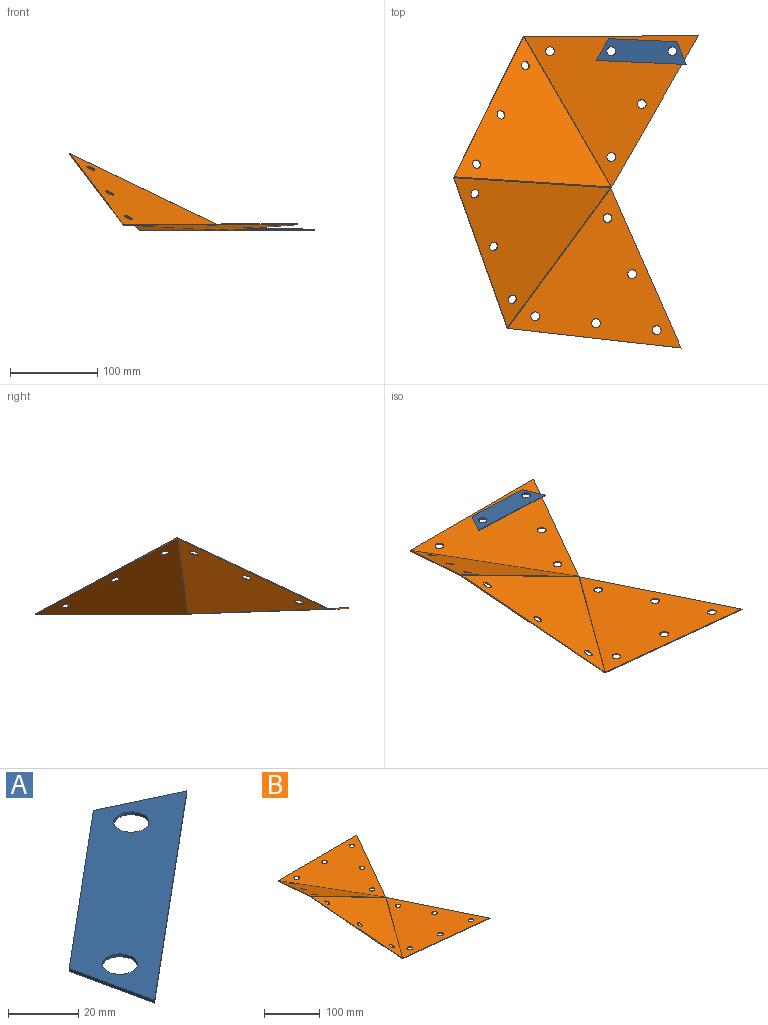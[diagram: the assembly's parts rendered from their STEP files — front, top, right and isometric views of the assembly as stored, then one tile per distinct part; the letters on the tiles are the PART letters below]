
ASSEMBLY  parts=2 mates=1
PART A: 8 faces, bbox 85.4x78.3x1 mm
  f0: plane 79.29x66.34mm, normal (0.64,-0.77,0), area 103.4mm2, adj f1,f4,f6,f7
  f1: plane 25.54x12mm, normal (0.43,0.91,0), area 28.2mm2, adj f0,f2,f6,f7
  f2: plane 59.9x50.18mm, normal (-0.64,0.77,0), area 78.1mm2, adj f1,f4,f6,f7
  f3: cylinder r=5mm len=10mm, axis (0,0,-1), area 31.4mm2, adj f6,f7
  f4: plane 28.16x6.15mm, normal (-0.98,-0.21,0), area 28.8mm2, adj f0,f2,f6,f7
  f5: cylinder r=5mm len=10mm, axis (0,0,-1), area 31.4mm2, adj f6,f7
  f6: plane 85.44x78.34mm, normal (0,0,1), area 2163.2mm2, adj f0,f1,f2,f3,f4,f5
  f7: plane 85.44x78.34mm, normal (0,0,-1), area 2163.2mm2, adj f0,f1,f2,f3,f4,f5
PART B: 46 faces, bbox 280.4x357.3x87.6 mm
  f0: plane 1x0.4mm, normal (-0.87,-0.5,0), area 0.5mm2, adj f1,f8,f9,f42
  f1: plane 173.03x99.68mm, normal (0.87,-0.5,0), area 199.7mm2, adj f0,f7,f8,f9
  f2: cylinder r=5mm len=10mm, axis (0,0,1), area 31.4mm2, adj f8,f9
  f3: cylinder r=5mm len=10mm, axis (0,0,1), area 31.4mm2, adj f8,f9
  f4: cylinder r=5mm len=10mm, axis (0,0,1), area 31.4mm2, adj f8,f9
  f5: cylinder r=5mm len=10mm, axis (0,0,1), area 31.4mm2, adj f8,f9
  f6: cylinder r=5mm len=10mm, axis (0,0,1), area 31.4mm2, adj f8,f9
  f7: plane 199.69x1mm, normal (0,1,0), area 199.7mm2, adj f1,f8,f9,f43
  f8: plane 199.69x173.03mm, normal (0,0,-1), area 16874.3mm2, adj f0,f1,f2,f3,f4,f5,f6,f7
  f9: plane 199.69x173.03mm, normal (0,0,1), area 16874.3mm2, adj f0,f1,f2,f3,f4,f5,f6,f7
  f10: plane 1.13x0.99mm, normal (0.06,-0.97,0.25), area 0.6mm2, adj f15,f16,f38,f42
  f11: plane 161.43x87.2mm, normal (-0.81,0.53,0.25), area 199.4mm2, adj f15,f16,f39,f43
  f12: cylinder r=5mm len=9.93mm, axis (-0.43,-0.25,-0.87), area 31.4mm2, adj f15,f16
  f13: cylinder r=5mm len=9.93mm, axis (-0.43,-0.25,-0.87), area 31.4mm2, adj f15,f16
  f14: cylinder r=5mm len=9.93mm, axis (-0.43,-0.25,-0.87), area 31.4mm2, adj f15,f16
  f15: plane 179.36x172.57mm, normal (-0.43,-0.25,-0.87), area 16977.9mm2, adj f10,f11,f12,f13,f14,f41,f44
  f16: plane 179.36x172.57mm, normal (0.43,0.25,0.87), area 16977.9mm2, adj f10,f11,f12,f13,f14,f40,f45
  f17: plane 1.01x0.68mm, normal (0.17,0.96,0.22), area 0.3mm2, adj f18,f19,f23,f39
  f18: plane 179.27x171.84mm, normal (0.4,-0.27,0.87), area 16977.9mm2, adj f17,f19,f20,f21,f22,f24,f37,f40
  f19: plane 172.1x81.43mm, normal (-0.86,-0.43,0.27), area 199.4mm2, adj f17,f18,f23,f34
  f20: cylinder r=5mm len=9.91mm, axis (-0.4,0.27,-0.87), area 31.4mm2, adj f18,f23
  f21: cylinder r=5mm len=9.91mm, axis (-0.4,0.27,-0.87), area 31.4mm2, adj f18,f23
  f22: cylinder r=5mm len=9.91mm, axis (-0.4,0.27,-0.87), area 31.4mm2, adj f18,f23
  f23: plane 179.27x171.84mm, normal (-0.4,0.27,-0.87), area 16977.9mm2, adj f17,f19,f20,f21,f22,f24,f36,f41
  f24: plane 1x0.59mm, normal (0.59,0.8,-0.03), area 0.3mm2, adj f18,f23,f35,f38
  f25: plane 183.01x80.5mm, normal (0.92,0.4,-0.02), area 200mm2, adj f26,f32,f33,f35
  f26: plane 198.73x22.57mm, normal (-0.11,-0.99,0.03), area 200mm2, adj f25,f32,f33,f34
  f27: cylinder r=5mm len=10.03mm, axis (0,-0.03,-1), area 31.4mm2, adj f32,f33
  f28: cylinder r=5mm len=10.03mm, axis (0,-0.03,-1), area 31.4mm2, adj f32,f33
  f29: cylinder r=5mm len=10.03mm, axis (0,-0.03,-1), area 31.4mm2, adj f32,f33
  f30: cylinder r=5mm len=10.03mm, axis (0,-0.03,-1), area 31.4mm2, adj f32,f33
  f31: cylinder r=5mm len=10.03mm, axis (0,-0.03,-1), area 31.4mm2, adj f32,f33
  f32: plane 198.73x182.98mm, normal (0,-0.03,-1), area 16892mm2, adj f25,f26,f27,f28,f29,f30,f31,f36
  f33: plane 198.73x182.98mm, normal (0,0.03,1), area 16892mm2, adj f25,f26,f27,f28,f29,f30,f31,f37
  f34: bspline ~1.12x0.73mm, area 0.8mm2, adj f19,f26,f36,f37
  f35: plane 1.12x0.81mm, normal (0.59,0.8,-0.03), area 0.8mm2, adj f24,f25,f36,f37
  f36: cylinder r=2mm len=161.05mm, axis (-0.59,-0.8,0.03), area 208.7mm2, adj f23,f32,f34,f35
  f37: cylinder r=1mm len=160.74mm, axis (-0.59,-0.8,0.03), area 104.4mm2, adj f18,f33,f34,f35
  f38: plane 1.03x0.94mm, normal (0.9,-0.06,-0.43), area 0.8mm2, adj f10,f24,f40,f41
  f39: plane 1.03x0.94mm, normal (-0.9,0.06,0.43), area 0.8mm2, adj f11,f17,f40,f41
  f40: cylinder r=2mm len=178.87mm, axis (0.9,-0.06,-0.43), area 208.1mm2, adj f16,f18,f38,f39
  f41: cylinder r=1mm len=178.83mm, axis (0.9,-0.06,-0.43), area 104.1mm2, adj f15,f23,f38,f39
  f42: plane 1.13x0.87mm, normal (0.5,-0.87,0), area 0.8mm2, adj f0,f10,f44,f45
  f43: bspline ~1.13x0.94mm, area 0.8mm2, adj f7,f11,f44,f45
  f44: cylinder r=2mm len=173.07mm, axis (0.5,-0.87,0), area 208.7mm2, adj f8,f15,f42,f43
  f45: cylinder r=1mm len=172.82mm, axis (0.5,-0.87,0), area 104.4mm2, adj f9,f16,f42,f43
PLACE A rot(axis=(0,0,-1),42.5deg) t=(69.08,242.36,-14.64)mm
PLACE B t=(34.14,222.25,-15.64)mm
MATE revolute A.f5 <-> B.f5  axis (0,0,-1) through (34.14,262.66,-14.64)mm
